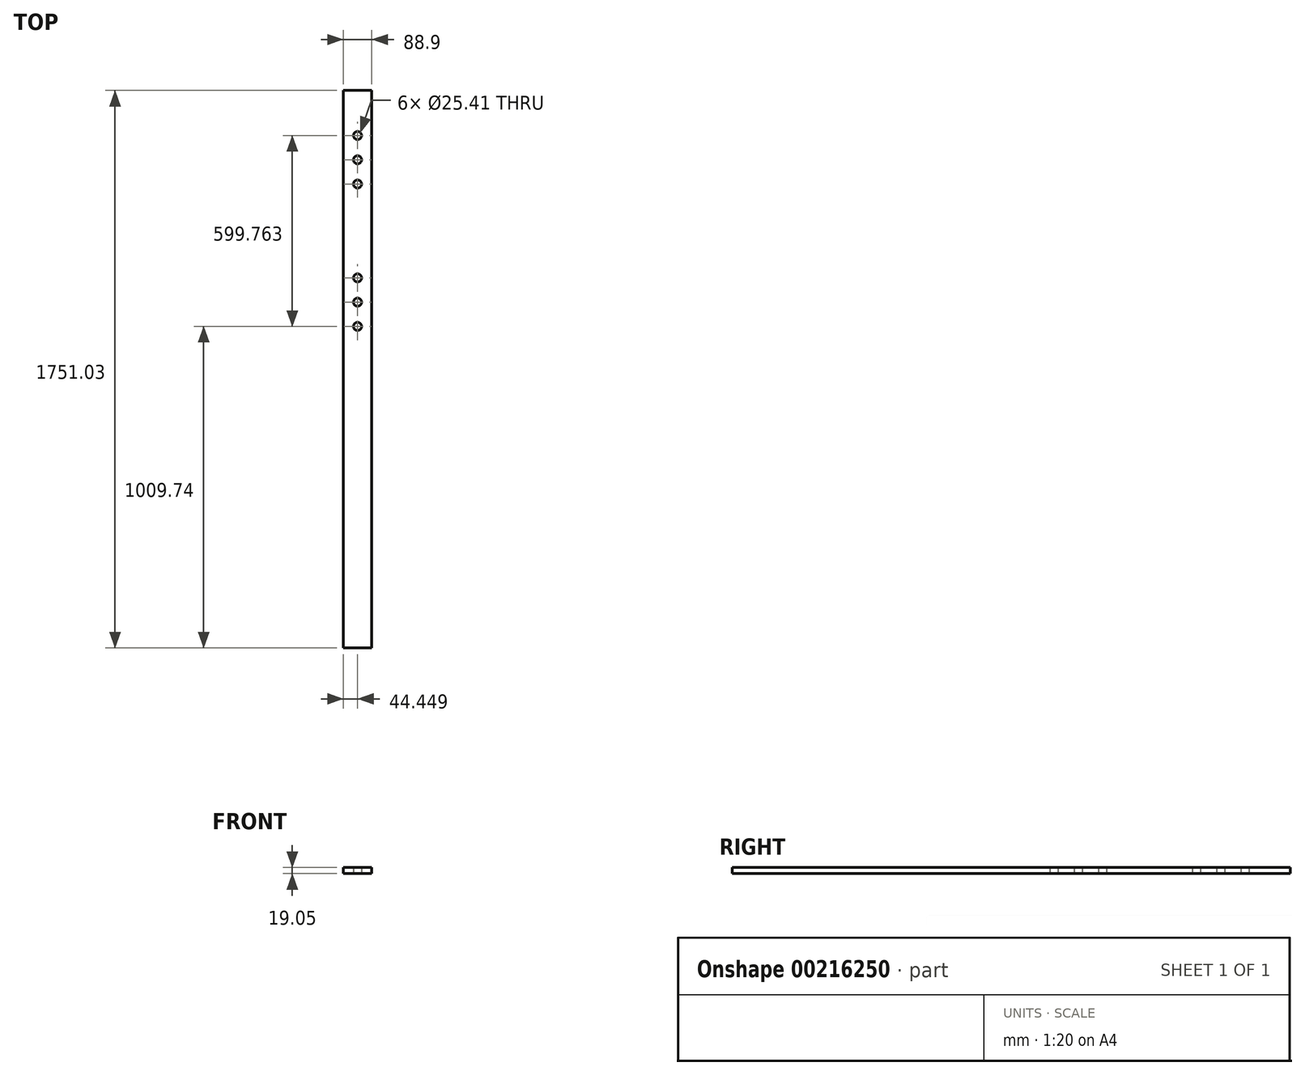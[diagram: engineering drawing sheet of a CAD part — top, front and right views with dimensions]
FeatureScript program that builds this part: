
annotation { "Feature Type Name" : "Feature", "Feature Type Description" : "" }
export const myFeature = defineFeature(function(context is Context, id is Id, definition is map)
    precondition{}
    {
        {
            var Q0;
            Q0=qCreatedBy(makeId("Top.planeOp"),FACE);
            var sketch = newSketch(context, id + "F0", { "sketchPlane" : qUnion([Q0])});
            skLineSegment(sketch, "E0", {"start": v(-1868.15, -362.65) * mm, "end": v(-1779.25, -362.65) * mm});
            skLineSegment(sketch, "E1", {"start": v(-1779.25, -362.65) * mm, "end": v(-1779.25, -2113.68) * mm});
            skLineSegment(sketch, "E2", {"start": v(-1779.25, -2113.68) * mm, "end": v(-1868.15, -2113.68) * mm});
            skLineSegment(sketch, "E3", {"start": v(-1868.15, -2113.68) * mm, "end": v(-1868.15, -362.65) * mm});
            skCircle(sketch, "E4", {"center": v(-1823.7, -951.47) * mm, "radius": 12.7 * mm});
            skCircle(sketch, "E5", {"center": v(-1823.7, -1027.7) * mm, "radius": 12.7 * mm});
            skCircle(sketch, "E6", {"center": v(-1823.7, -1103.94) * mm, "radius": 12.7 * mm});
            skCircle(sketch, "E7", {"center": v(-1823.7, -656.68) * mm, "radius": 12.7 * mm});
            skCircle(sketch, "E8", {"center": v(-1823.7, -580.47) * mm, "radius": 12.7 * mm});
            skCircle(sketch, "E9", {"center": v(-1823.7, -504.17) * mm, "radius": 12.7 * mm});
            skSolve(sketch);
        }
        {
            var Q0;
            Q0=makeQuery(id+"F0.imprint","IMPRINT",FACE,{"disambiguationData":[TD([[makeQuery(id+"F0.imprint","IMPRINT",EDGE,{"derivedFrom":sQuery(id+"F0.wireOp",EDGE,"E0")}),-1.0]])]});
            extrude(context, id + "F1", {"entities" : qUnion([Q0]), "depth" : 19.05 * mm});
        }
    });
